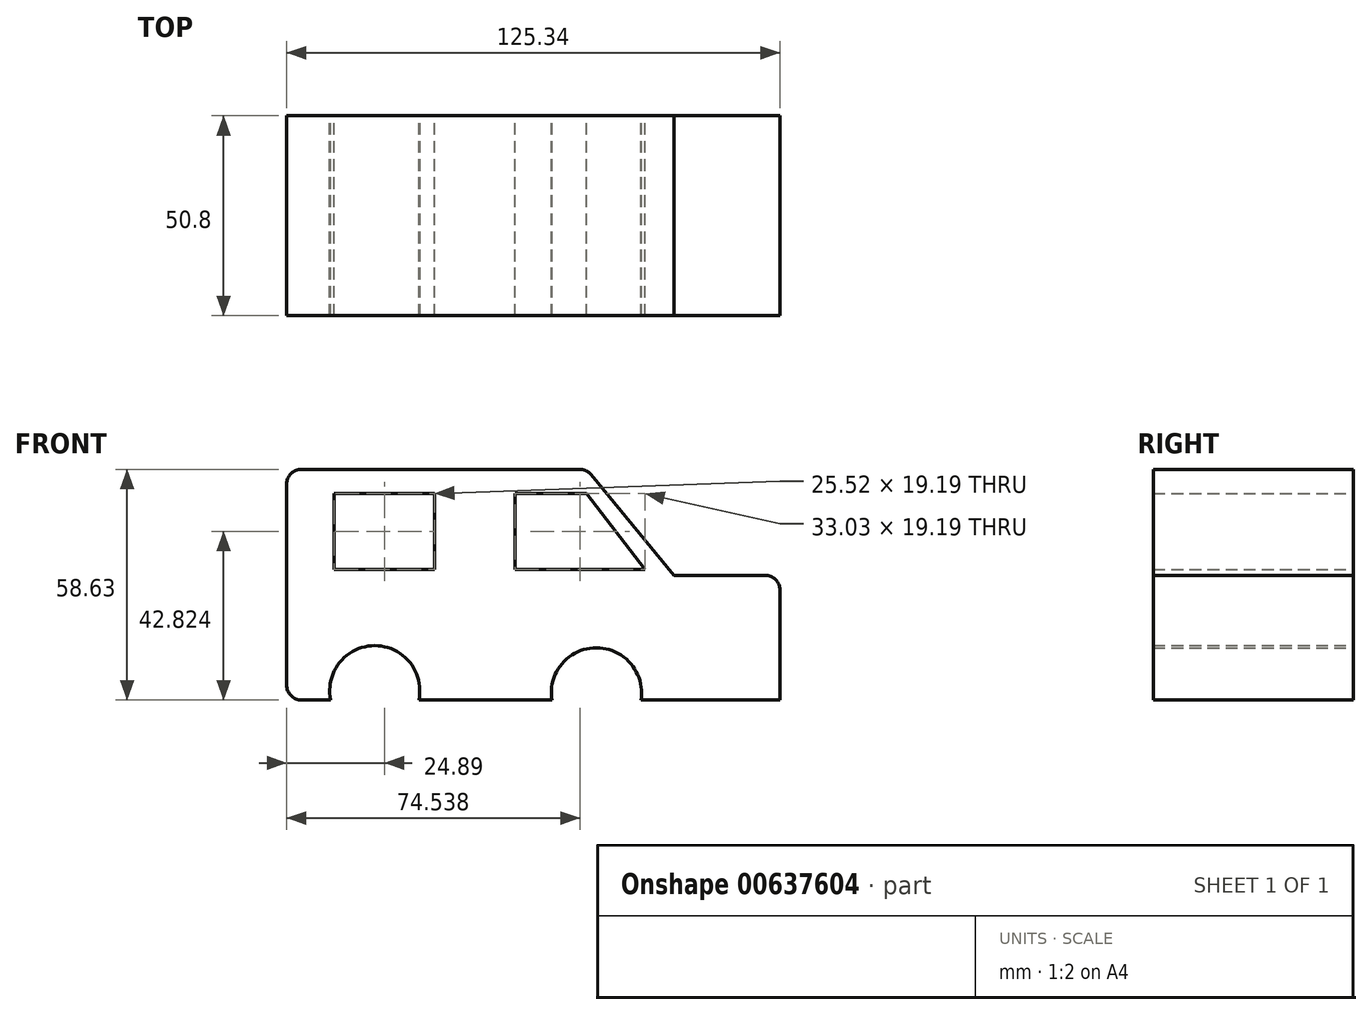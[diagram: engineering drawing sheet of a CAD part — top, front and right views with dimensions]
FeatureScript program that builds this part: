
annotation { "Feature Type Name" : "Feature", "Feature Type Description" : "" }
export const myFeature = defineFeature(function(context is Context, id is Id, definition is map)
    precondition{}
    {
        {
            var Q0;
            Q0=qCreatedBy(makeId("Front.planeOp"),FACE);
            var sketch = newSketch(context, id + "F0", { "sketchPlane" : qUnion([Q0])});
            skLineSegment(sketch, "E0", {"start": v(-76.24, 54.82) * mm, "end": v(-76.24, 3.81) * mm});
            skLineSegment(sketch, "E1", {"start": v(-72.43, 58.63) * mm, "end": v(-1.8, 58.63) * mm});
            skLineSegment(sketch, "E2", {"start": v(1.14, 57.24) * mm, "end": v(22.18, 31.7) * mm});
            skLineSegment(sketch, "E3", {"start": v(22.18, 31.7) * mm, "end": v(45.3, 31.7) * mm});
            skLineSegment(sketch, "E4", {"start": v(49.1, 27.9) * mm, "end": v(49.1, 0) * mm});
            skLineSegment(sketch, "E5", {"start": v(49.1, 0) * mm, "end": v(-72.43, 0) * mm});
            skArc(sketch, "E6", {"start": v(-42.64, 0) * mm, "mid": v(-53.84, 13.82) * mm, "end": v(-65.04, 0) * mm});
            skArc(sketch, "E7", {"start": v(13.78, 0) * mm, "mid": v(2.48, 13.27) * mm, "end": v(-8.83, 0) * mm});
            skPoint(sketch, "E8.visualSharp", {"position": v(-76.24, 58.63) * mm});
            skArc(sketch, "E8.filletArc", {"start": v(-72.43, 58.63) * mm, "mid": v(-75.13, 57.5) * mm, "end": v(-76.24, 54.82) * mm});
            skPoint(sketch, "E9.visualSharp", {"position": v(0, 58.63) * mm});
            skArc(sketch, "E9.filletArc", {"start": v(1.14, 57.24) * mm, "mid": v(-0.17, 58.26) * mm, "end": v(-1.8, 58.63) * mm});
            skPoint(sketch, "E10.visualSharp", {"position": v(49.1, 31.7) * mm});
            skArc(sketch, "E10.filletArc", {"start": v(49.1, 27.9) * mm, "mid": v(47.99, 30.59) * mm, "end": v(45.3, 31.7) * mm});
            skPoint(sketch, "E11.visualSharp", {"position": v(-76.24, 0) * mm});
            skArc(sketch, "E11.filletArc", {"start": v(-76.24, 3.81) * mm, "mid": v(-75.13, 1.12) * mm, "end": v(-72.43, 0) * mm});
            skLineSegment(sketch, "E12", {"start": v(-18.22, 52.42) * mm, "end": v(0, 52.42) * mm});
            skLineSegment(sketch, "E13", {"start": v(0, 52.42) * mm, "end": v(14.81, 33.23) * mm});
            skLineSegment(sketch, "E14", {"start": v(-18.22, 52.42) * mm, "end": v(-18.22, 33.23) * mm});
            skLineSegment(sketch, "E15", {"start": v(-18.22, 33.23) * mm, "end": v(14.81, 33.23) * mm});
            skLineSegment(sketch, "E16", {"start": v(-64.1, 52.42) * mm, "end": v(-38.6, 52.42) * mm});
            skLineSegment(sketch, "E17", {"start": v(-38.6, 52.42) * mm, "end": v(-38.6, 33.23) * mm});
            skLineSegment(sketch, "E18", {"start": v(-64.1, 52.42) * mm, "end": v(-64.1, 33.23) * mm});
            skLineSegment(sketch, "E19", {"start": v(-38.6, 33.23) * mm, "end": v(-64.1, 33.23) * mm});
            skSolve(sketch);
        }
        {
            var Q0;
            Q0=makeQuery(id+"F0.imprint","IMPRINT",FACE,{"disambiguationData":[TD([[makeQuery(id+"F0.imprint","IMPRINT",EDGE,{"derivedFrom":sQuery(id+"F0.wireOp",EDGE,"E0")}),1.0]])]});
            extrude(context, id + "F1", {"entities" : qUnion([Q0]), "depth" : 50.8 * mm, "offsetDistance" : 25.4 * mm});
        }
    });
